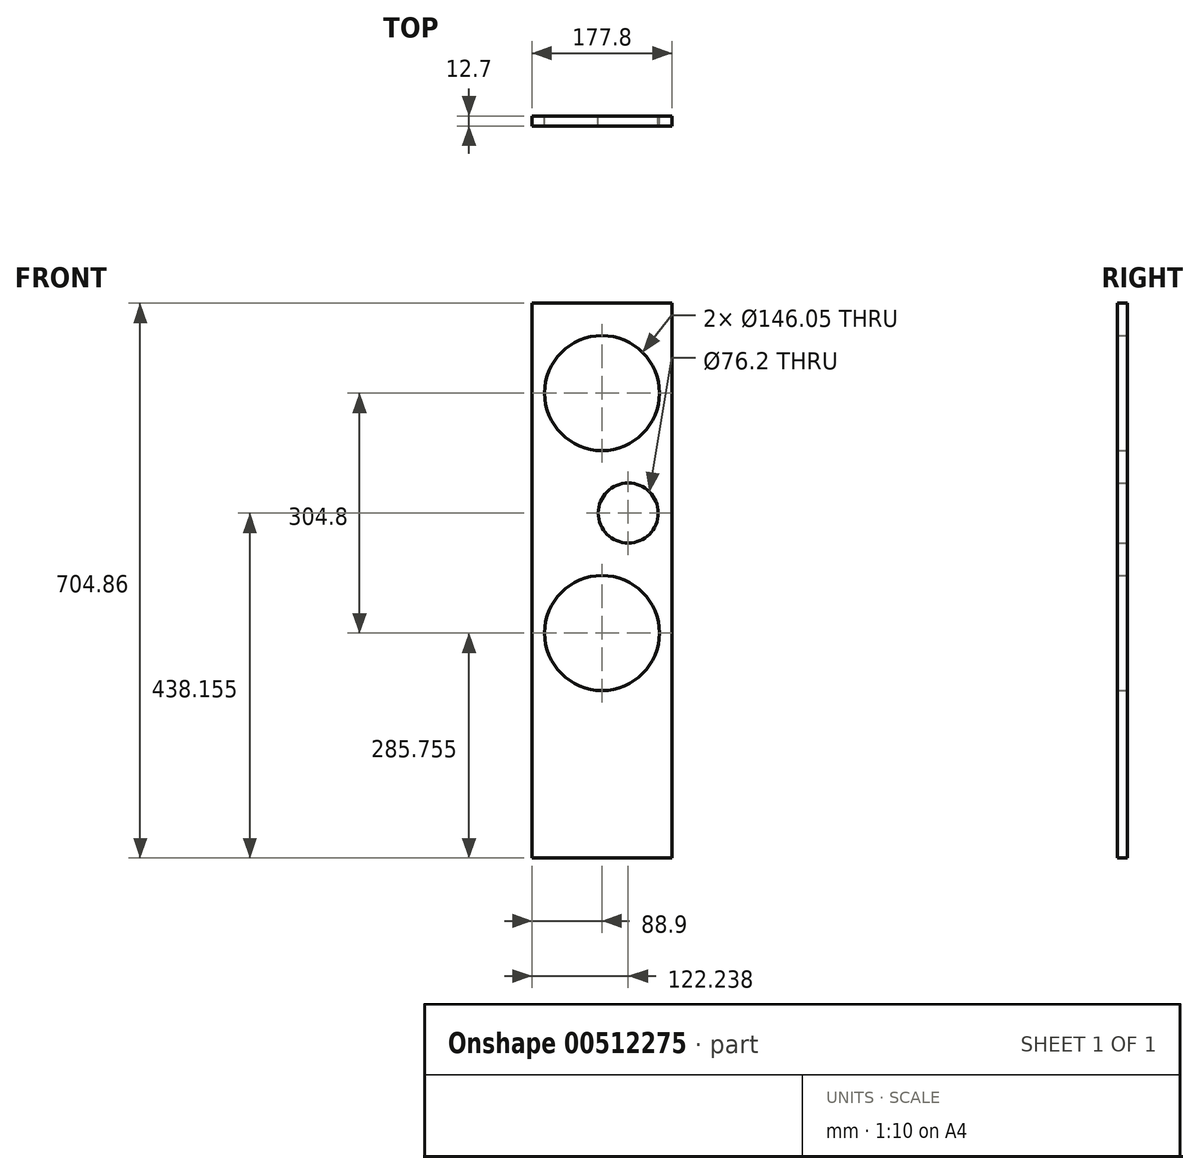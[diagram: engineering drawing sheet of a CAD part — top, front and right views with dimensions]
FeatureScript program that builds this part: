
annotation { "Feature Type Name" : "Feature", "Feature Type Description" : "" }
export const myFeature = defineFeature(function(context is Context, id is Id, definition is map)
    precondition{}
    {
        {
            var Q0;
            Q0=qCreatedBy(makeId("Front.planeOp"),FACE);
            var sketch = newSketch(context, id + "F0", { "sketchPlane" : qUnion([Q0])});
            skLineSegment(sketch, "E0.bottom", {"start": v(-88.9, 352.43) * mm, "end": v(88.9, 352.43) * mm});
            skLineSegment(sketch, "E0.top", {"start": v(-88.9, -352.43) * mm, "end": v(88.9, -352.43) * mm});
            skLineSegment(sketch, "E0.left", {"start": v(-88.9, 352.43) * mm, "end": v(-88.9, -352.43) * mm});
            skLineSegment(sketch, "E0.right", {"start": v(88.9, 352.43) * mm, "end": v(88.9, -352.43) * mm});
            skLineSegment(sketch, "E1", {"start": v(-88.9, 425.45) * mm, "end": v(88.9, 425.45) * mm});
            skLineSegment(sketch, "E2", {"start": v(-88.9, -488.95) * mm, "end": v(88.9, -488.95) * mm});
            skLineSegment(sketch, "E3", {"start": v(-88.9, 403.23) * mm, "end": v(88.9, 403.23) * mm});
            skLineSegment(sketch, "E4", {"start": v(-88.9, -403.23) * mm, "end": v(88.9, -403.23) * mm});
            skPoint(sketch, "E5", {"position": v(0, 238.13) * mm});
            skPoint(sketch, "E6", {"position": v(0, -66.67) * mm});
            skPoint(sketch, "E7", {"position": v(33.34, 85.73) * mm});
            skLineSegment(sketch, "E8", {"start": v(33.34, 85.73) * mm, "end": v(12.8, 85.73) * mm});
            skCircle(sketch, "E9", {"center": v(0, 238.13) * mm, "radius": 73.03 * mm});
            skCircle(sketch, "E10", {"center": v(0, -66.67) * mm, "radius": 73.03 * mm});
            skCircle(sketch, "E11", {"center": v(33.34, 85.73) * mm, "radius": 38.1 * mm});
            skLineSegment(sketch, "E12", {"start": v(241.73, 165.1) * mm, "end": v(345.42, 165.1) * mm});
            skLineSegment(sketch, "E13", {"start": v(236.34, 123.83) * mm, "end": v(366.97, 123.83) * mm});
            skLineSegment(sketch, "E14", {"start": v(247.12, 144.46) * mm, "end": v(319.84, 144.46) * mm});
            skLineSegment(sketch, "E15", {"start": v(228.62, 26.99) * mm, "end": v(310.04, 26.99) * mm});
            skLineSegment(sketch, "E16", {"start": v(223.06, -66.67) * mm, "end": v(318.74, -66.67) * mm});
            skLineSegment(sketch, "E17", {"start": v(224.79, -160.34) * mm, "end": v(322.18, -160.34) * mm});
            skSolve(sketch);
        }
        {
            var Q0;
            Q0=makeQuery(id+"F0.imprint","IMPRINT",FACE,{"disambiguationData":[TD([[makeQuery(id+"F0.imprint","IMPRINT",EDGE,{"derivedFrom":sQuery(id+"F0.wireOp",EDGE,"E0.bottom")}),-1.0]])]});
            extrude(context, id + "F1", {"entities" : qUnion([Q0]), "depth" : 12.7 * mm});
        }
    });
